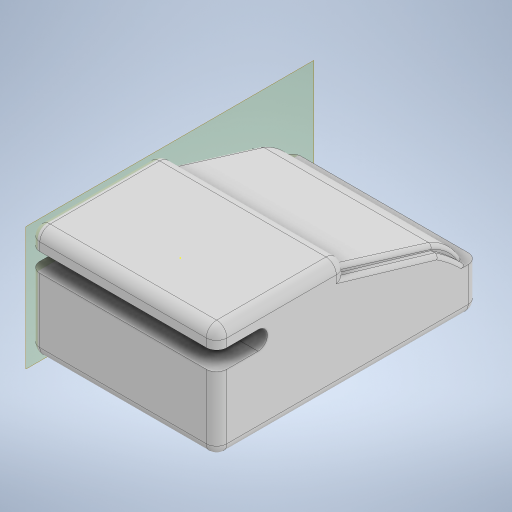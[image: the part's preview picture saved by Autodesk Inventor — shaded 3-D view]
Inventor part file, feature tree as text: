
AUTODESK INVENTOR PART (.ipt)
format: ipt  version: 2024 (Build 280153000, 153)  size: 365,568 bytes
history: native  units: in
note: dims shown in document units (in); Inventor stores cm internally (conversion verified against a paired STEP export)
features: sketch x6, extrude x5, fillet x5, plane x1
ambient origin geometry x8: Origin, YZ Plane, XZ Plane, XY Plane, X Axis, Y Axis, Z Axis, Center Point
bodies: Solid1 (feature_tree)
feature tree (17):
  extrude  "Extrusion1"  Depth=50.0in
  extrude  "Extrusion2"  Depth=70.0in
  fillet  "Fillet1"  Radius=12.0in
  fillet  "Fillet2"  Radius=70.0in
  extrude  "Extrusion3"  Depth=2.7559in
  fillet  "Fillet3"  Radius=50.0in
  fillet  "Fillet4"  Radius=1.0in
  plane  "Work Plane1"
  extrude  "Extrusion4"  Depth=1.0in TaperAngle=0.0deg
  sketch  "Sketch7"  dims[d21=5.0in d22=5.0in]
  fillet  "Fillet8"  Radius=1.0in
  extrude  "Extrusion5"  Depth=5.0in
  sketch  "Sketch1"  dims[d1=30.0in d2=50.0in]
  sketch  "Sketch2"  dims[d3=70.0in d4=0.0in d5=35.0in d6=12.0in d7=70.0in d8=0.0in]
  sketch  "Sketch3"  dims[d9=2.7559in d10=2.7559in d11=50.0in d12=0.0in d13=1.0in]
  sketch  "Sketch6"  dims[d14=3.0in d15=46.0in d16=0.0in d20=1.0in]
  sketch  "Sketch8"  dims[d23=50.0in d24=0.0in d17=0.0in d18=0.0in d19=0.0in]
